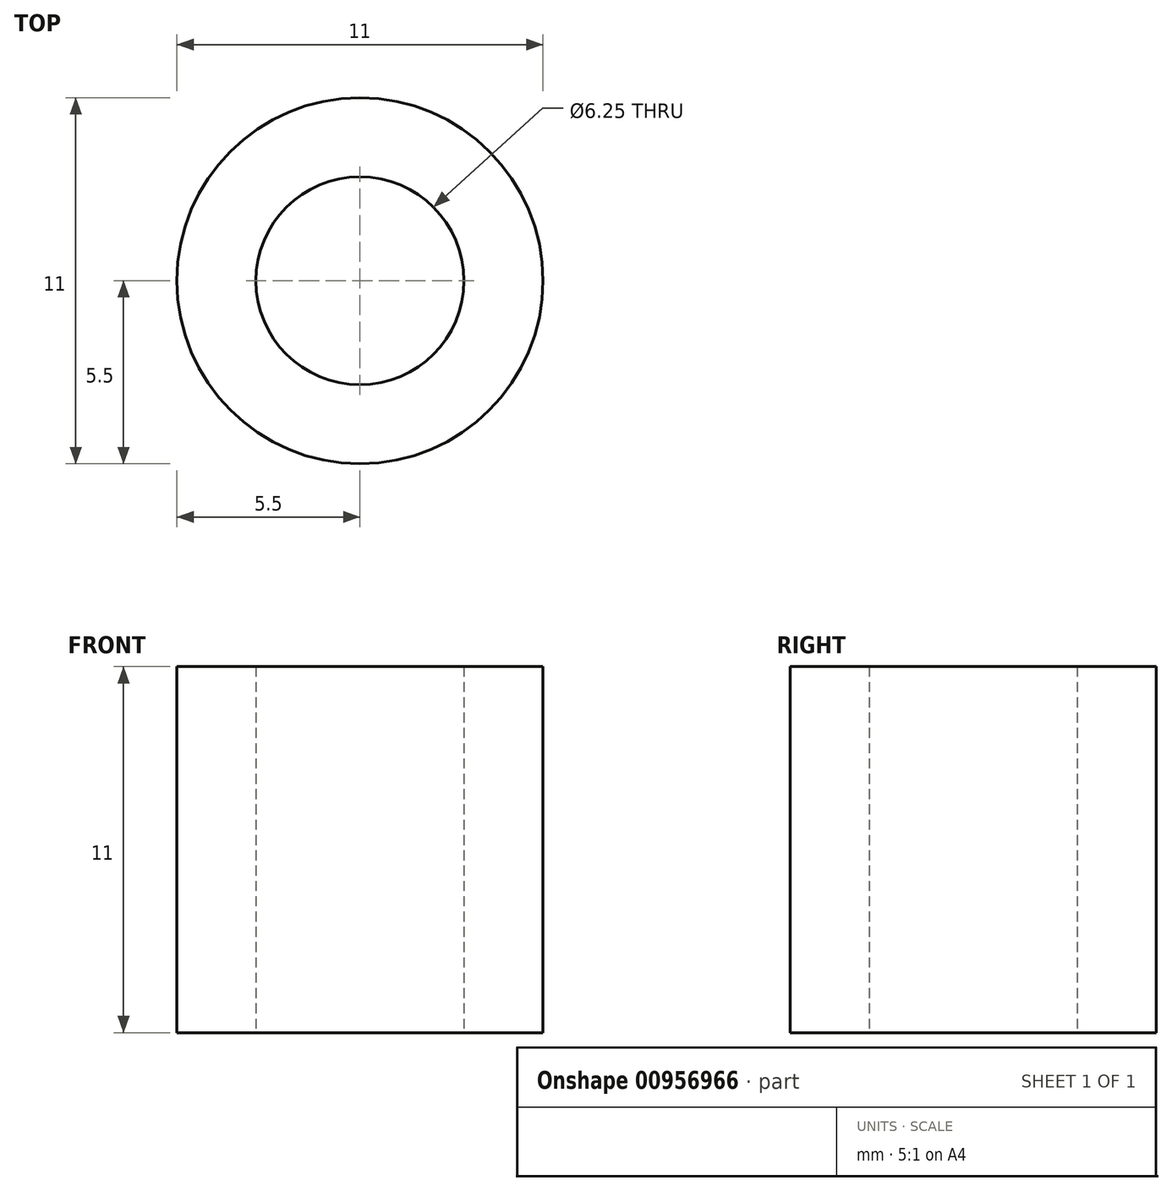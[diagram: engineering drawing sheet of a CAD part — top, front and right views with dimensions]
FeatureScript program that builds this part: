
annotation { "Feature Type Name" : "Feature", "Feature Type Description" : "" }
export const myFeature = defineFeature(function(context is Context, id is Id, definition is map)
    precondition{}
    {
        {
            var Q0;
            Q0=qCreatedBy(makeId("Top.planeOp"),FACE);
            var sketch = newSketch(context, id + "F0", { "sketchPlane" : qUnion([Q0])});
            skCircle(sketch, "E0", {"center": v(0, 0) * mm, "radius": 5.5 * mm});
            skCircle(sketch, "E1", {"center": v(0, 0) * mm, "radius": 3.12 * mm});
            skSolve(sketch);
        }
        {
            var Q0;
            Q0=makeQuery(id+"F0.imprint","IMPRINT",FACE,{"disambiguationData":[TD([[makeQuery(id+"F0.imprint","IMPRINT",EDGE,{"derivedFrom":sQuery(id+"F0.wireOp",EDGE,"E0")}),1.0]])]});
            extrude(context, id + "F1", {"entities" : qUnion([Q0]), "depth" : 11 * mm, "offsetDistance" : 25 * mm});
        }
    });
